# Revit family: Door_Swing_DORMA_Studio
name_source: partatom
category: Türen
revit_build: Autodesk Revit 2013 (Build: 20120221_2030(x64)
units: mm (PartAtom-declared; Revit-internal decimal feet)

## types (6) — shared parameters
Bauelement = L20
Baugruppenkennzeichen = C1020100
Default Handle Elevation = 1068 mm  [stored 3.50394 ft]
Door Frame Material = <Nach Kategorie>
Door Panel Height = 2079 mm
Door Panel Material = Glass
Door Panel Thickness = 10 mm  [stored 0.0328084 ft]
Frame Projection Ext. = 25 mm  [stored 0.082021 ft]
Frame Projection Int. = 25 mm  [stored 0.082021 ft]
Frame Width = 75 mm  [stored 0.246063 ft]
Funktion = Innen
Hersteller = DORMA
Höhe = 2100 mm
Material = E.g- Core Material
Modell = Swing Doorset Studio
Undercut = 8 mm  [stored 0.0262467 ft]
Wandabschluss = Nach Basisbauteil
_current revision = 1
zero-valued in all types: Barcode, NominalHeight, NominalWidth, SerialNumber, WarrentyDuration

## per-type parameters (varying)
| type | Breite | Door Panel Width | Handle Type |
| STUDIO CLASSIC | 1000 mm  [stored 3.28084 ft] | 973 mm | Ironmongery-Door_Handle-Studio_CLASSIC : CLASSIC |
| MEDIO | 1000 mm  [stored 3.28084 ft] | 973 mm | Ironmongery-Door_Handle-Studio_MEDIO : MEDIO |
| JUNIOR OFFICE | 1000 mm  [stored 3.28084 ft] | 973 mm | Ironmongery-Door_Handle-Studio_JUNIOR_OFFICE : JUNIOR OFFICE |
| JUNIOR OFFICE CLASSIC | 1000 mm  [stored 3.28084 ft] | 973 mm | Ironmongery-Door_Handle-Studio_JUNIOR_OFFICE_CLASSIC : JUNIOR OFFICE CLASSIC |
| STUIDIO RONDO | 1500 mm  [stored 4.92126 ft] | 1473 mm  [stored 4.83268 ft] | Ironmongery-Door_Handle-Studio_RONDO : RONDO |
| STUDIO GALA | 1000 mm  [stored 3.28084 ft] | 973 mm | Ironmongery-Door_Handle-Studio_GALA : GALA |

note: [stored X ft] marks values corroborated as IEEE doubles in the binary element streams (Revit-internal decimal feet)

## geometry (parser evidence)
native form markers: Blend x32, Sweep x54
no freeform markers — native parametric forms only
